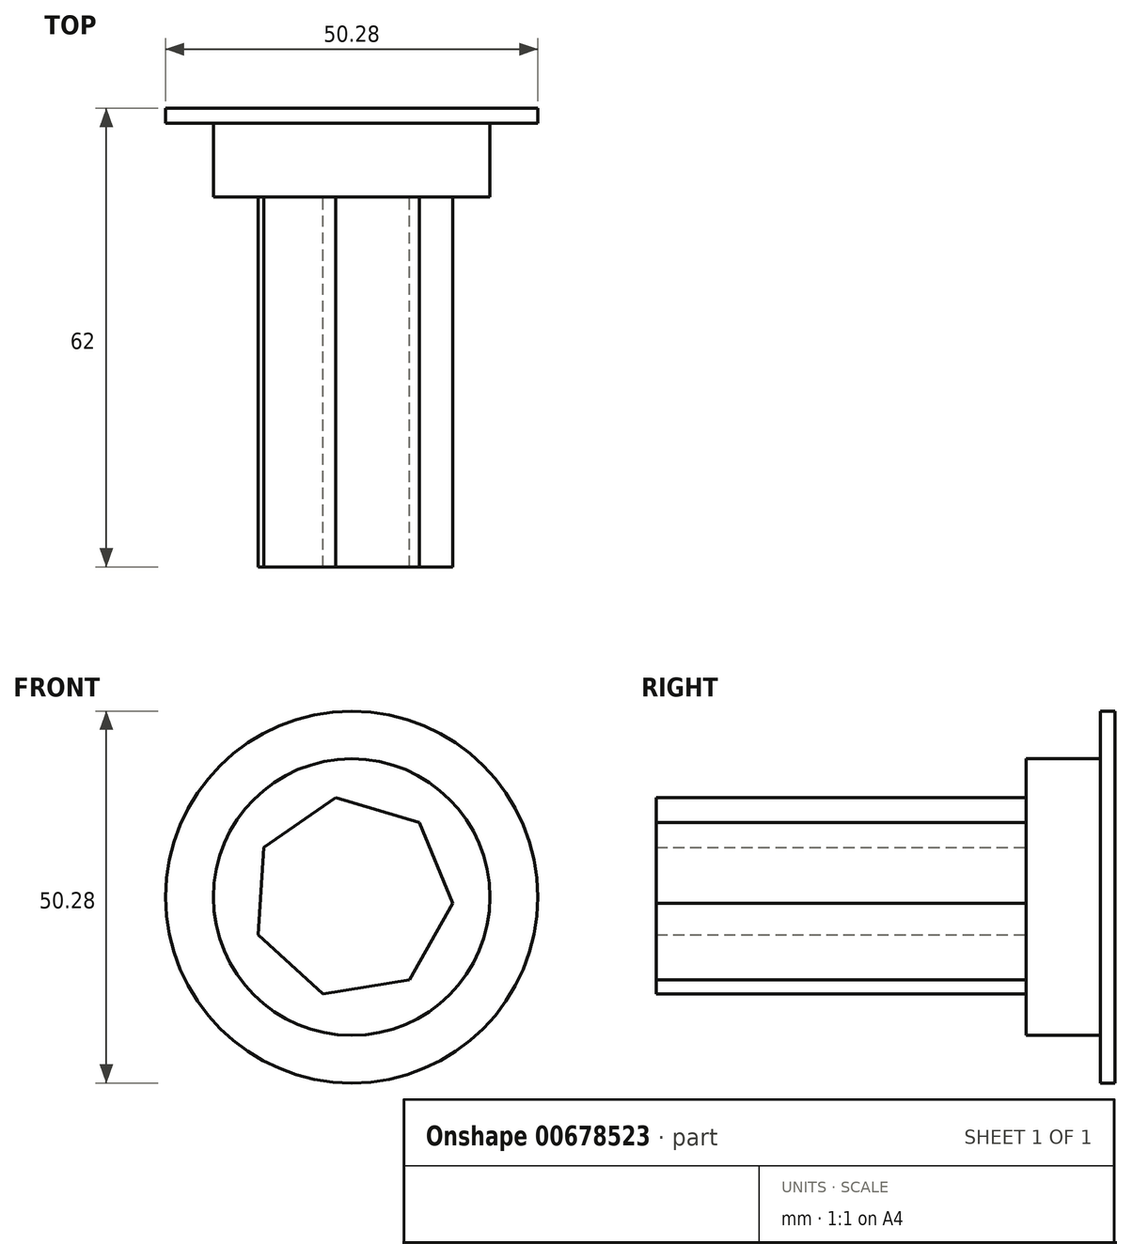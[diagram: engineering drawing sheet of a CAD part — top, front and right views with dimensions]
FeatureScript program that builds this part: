
annotation { "Feature Type Name" : "Feature", "Feature Type Description" : "" }
export const myFeature = defineFeature(function(context is Context, id is Id, definition is map)
    precondition{}
    {
        {
            var Q0;
            Q0=qCreatedBy(makeId("Front.planeOp"),FACE);
            var sketch = newSketch(context, id + "F0", { "sketchPlane" : qUnion([Q0])});
            skCircle(sketch, "E0", {"center": v(0, 0) * mm, "radius": 25.14 * mm});
            skSolve(sketch);
        }
        {
            var Q0;
            Q0=makeQuery(id+"F0.imprint","IMPRINT",FACE,{"disambiguationData":[TD([[makeQuery(id+"F0.imprint","IMPRINT",EDGE,{"derivedFrom":sQuery(id+"F0.wireOp",EDGE,"E0")}),1.0]])]});
            extrude(context, id + "F1", {"entities" : qUnion([Q0]), "depth" : 2 * mm, "offsetDistance" : 25 * mm});
        }
        {
            var Q0;
            Q0=makeQuery(id+"F1.opExtrude","CAP_FACE",FACE,{"disambiguationData":[OSD([sQuery(id+"F0.wireOp",EDGE,"E0")])],"isStart":false});
            var sketch = newSketch(context, id + "F2", { "sketchPlane" : qUnion([Q0])});
            skCircle(sketch, "E1", {"center": v(0, 0) * mm, "radius": 18.7 * mm});
            skSolve(sketch);
        }
        {
            var Q0;
            Q0=makeQuery(id+"F2.imprint","IMPRINT",FACE,{"disambiguationData":[TD([[makeQuery(id+"F2.imprint","IMPRINT",EDGE,{"derivedFrom":sQuery(id+"F2.wireOp",EDGE,"E1")}),1.0]])]});
            extrude(context, id + "F3", {"entities" : qUnion([Q0]), "operationType" : NewBodyOperationType.ADD, "depth" : 10 * mm, "offsetDistance" : 25 * mm});
        }
        {
            var Q0;
            Q0=makeQuery(id+"F3.opExtrude","CAP_FACE",FACE,{"disambiguationData":[OSD([sQuery(id+"F2.wireOp",EDGE,"E1")])],"isStart":false});
            var sketch = newSketch(context, id + "F4", { "sketchPlane" : qUnion([Q0])});
            skLineSegment(sketch, "E2.0", {"start": v(-3.88, -13.08) * mm, "end": v(-12.64, -5.13) * mm});
            skLineSegment(sketch, "E2.1", {"start": v(-12.64, -5.13) * mm, "end": v(-11.9, 6.69) * mm});
            skLineSegment(sketch, "E2.2", {"start": v(-11.9, 6.69) * mm, "end": v(-2.19, 13.47) * mm});
            skLineSegment(sketch, "E2.3", {"start": v(-2.19, 13.47) * mm, "end": v(9.17, 10.1) * mm});
            skLineSegment(sketch, "E2.4", {"start": v(9.17, 10.1) * mm, "end": v(13.62, -0.87) * mm});
            skLineSegment(sketch, "E2.5", {"start": v(13.62, -0.87) * mm, "end": v(7.81, -11.19) * mm});
            skLineSegment(sketch, "E2.6", {"start": v(7.81, -11.19) * mm, "end": v(-3.88, -13.08) * mm});
            skSolve(sketch);
        }
        {
            var Q0;
            Q0=makeQuery(id+"F4.imprint","IMPRINT",FACE,{"disambiguationData":[TD([[makeQuery(id+"F4.imprint","IMPRINT",EDGE,{"derivedFrom":sQuery(id+"F4.wireOp",EDGE,"E2.0")}),-1.0]])]});
            extrude(context, id + "F5", {"entities" : qUnion([Q0]), "operationType" : NewBodyOperationType.ADD, "depth" : 50 * mm, "offsetDistance" : 25 * mm});
        }
    });
